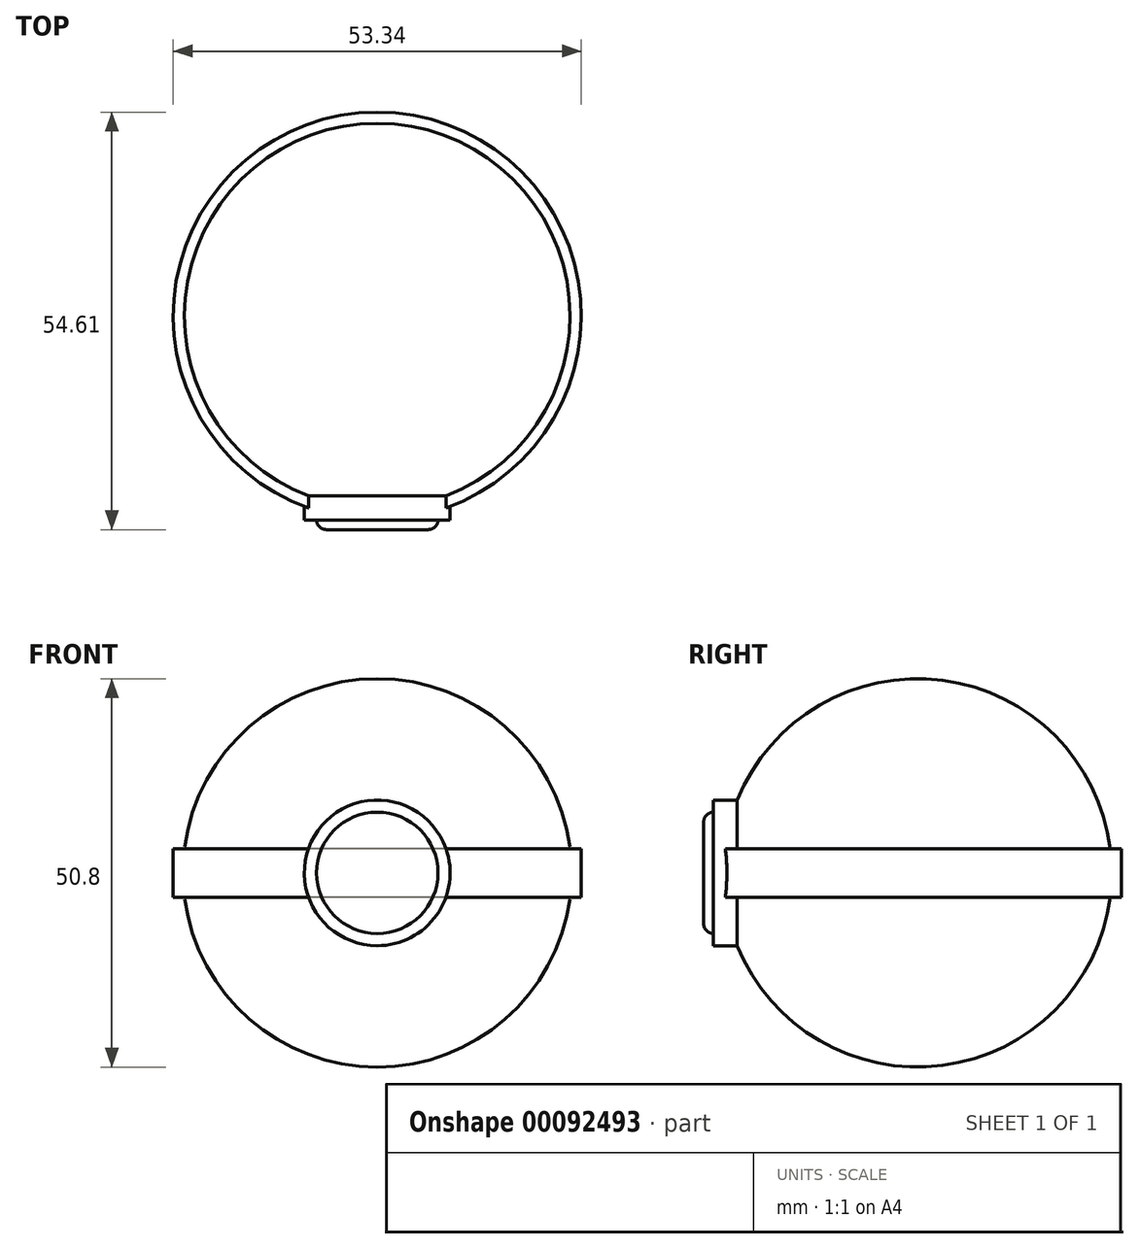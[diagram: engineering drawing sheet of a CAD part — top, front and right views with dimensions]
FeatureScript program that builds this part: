
annotation { "Feature Type Name" : "Feature", "Feature Type Description" : "" }
export const myFeature = defineFeature(function(context is Context, id is Id, definition is map)
    precondition{}
    {
        {
            var Q0;
            Q0=qCreatedBy(makeId("Front.planeOp"),FACE);
            var sketch = newSketch(context, id + "F0", { "sketchPlane" : qUnion([Q0])});
            skCircle(sketch, "E0", {"center": v(0, 0) * mm, "radius": 25.4 * mm});
            skLineSegment(sketch, "E1", {"start": v(-25.4, 0) * mm, "end": v(25.4, 0) * mm});
            skSolve(sketch);
        }
        {
            var Q0;
            {var subQ0=sQuery(id+"F0.wireOp",EDGE,"E1");Q0=makeQuery(id+"F0.imprint","IMPRINT",FACE,{"disambiguationData":[TD([[makeQuery(id+"F0.imprint","IMPRINT",EDGE,{"derivedFrom":subQ0}),-1.0]])]});}
            var Q1;
            Q1=sQuery(id+"F0.wireOp",EDGE,"E1");
            revolve(context, id + "F1", {"entities" : qUnion([Q0]), "axis" : qUnion([Q1]), "revolveType" : RevolveType.FULL});
        }
        {
            var Q0;
            Q0=qCreatedBy(makeId("Front.planeOp"),FACE);
            var sketch = newSketch(context, id + "F2", { "sketchPlane" : qUnion([Q0])});
            skCircle(sketch, "E2", {"center": v(0, 0) * mm, "radius": 7.94 * mm});
            skSolve(sketch);
        }
        {
            var Q0;
            Q0 = qSketchRegion(id + "F2", true);
            extrude(context, id + "F3", {"entities" : qUnion([Q0]), "operationType" : NewBodyOperationType.ADD, "depth" : 27.94 * mm});
        }
        {
            var Q0;
            Q0=makeQuery(id+"F3.opExtrude","CAP_FACE",FACE,{"disambiguationData":[OSD([sQuery(id+"F2.wireOp",EDGE,"E2")])],"isStart":false});
            var Q1;
            Q1=makeQuery(id+"F3.opExtrude","SWEPT_FACE",FACE,{"disambiguationData":[OSD([sQuery(id+"F2.wireOp",EDGE,"E2")])]});
            var Q2;
            Q2=makeQuery(id+"F1.opRevolve","SWEPT_FACE",FACE,{"disambiguationData":[OSD([sQuery(id+"F0.wireOp",EDGE,"E0")])]});
            fillet(context, id + "F4", {"entities" : qUnion([Q0, Q1, Q2]), "radius" : 1.27 * mm, "tangentPropagation" : true, "allowEdgeOverflow" : false});
        }
        {
            var Q0;
            Q0=qCreatedBy(makeId("Top.planeOp"),FACE);
            var sketch = newSketch(context, id + "F5", { "sketchPlane" : qUnion([Q0])});
            skCircle(sketch, "E3", {"center": v(0, 0) * mm, "radius": 26.67 * mm});
            skSolve(sketch);
        }
        {
            var Q0;
            Q0 = qSketchRegion(id + "F5", true);
            extrude(context, id + "F6", {"entities" : qUnion([Q0]), "operationType" : NewBodyOperationType.ADD, "endBound" : BoundingType.SYMMETRIC, "depth" : 6.35 * mm});
        }
        {
            var Q0;
            Q0=qCreatedBy(makeId("Front.planeOp"),FACE);
            var sketch = newSketch(context, id + "F7", { "sketchPlane" : qUnion([Q0])});
            skCircle(sketch, "E4", {"center": v(0, 0) * mm, "radius": 9.52 * mm});
            skSolve(sketch);
        }
        {
            var Q0;
            Q0 = qSketchRegion(id + "F7", true);
            extrude(context, id + "F8", {"entities" : qUnion([Q0]), "operationType" : NewBodyOperationType.ADD, "depth" : 26.67 * mm});
        }
    });
